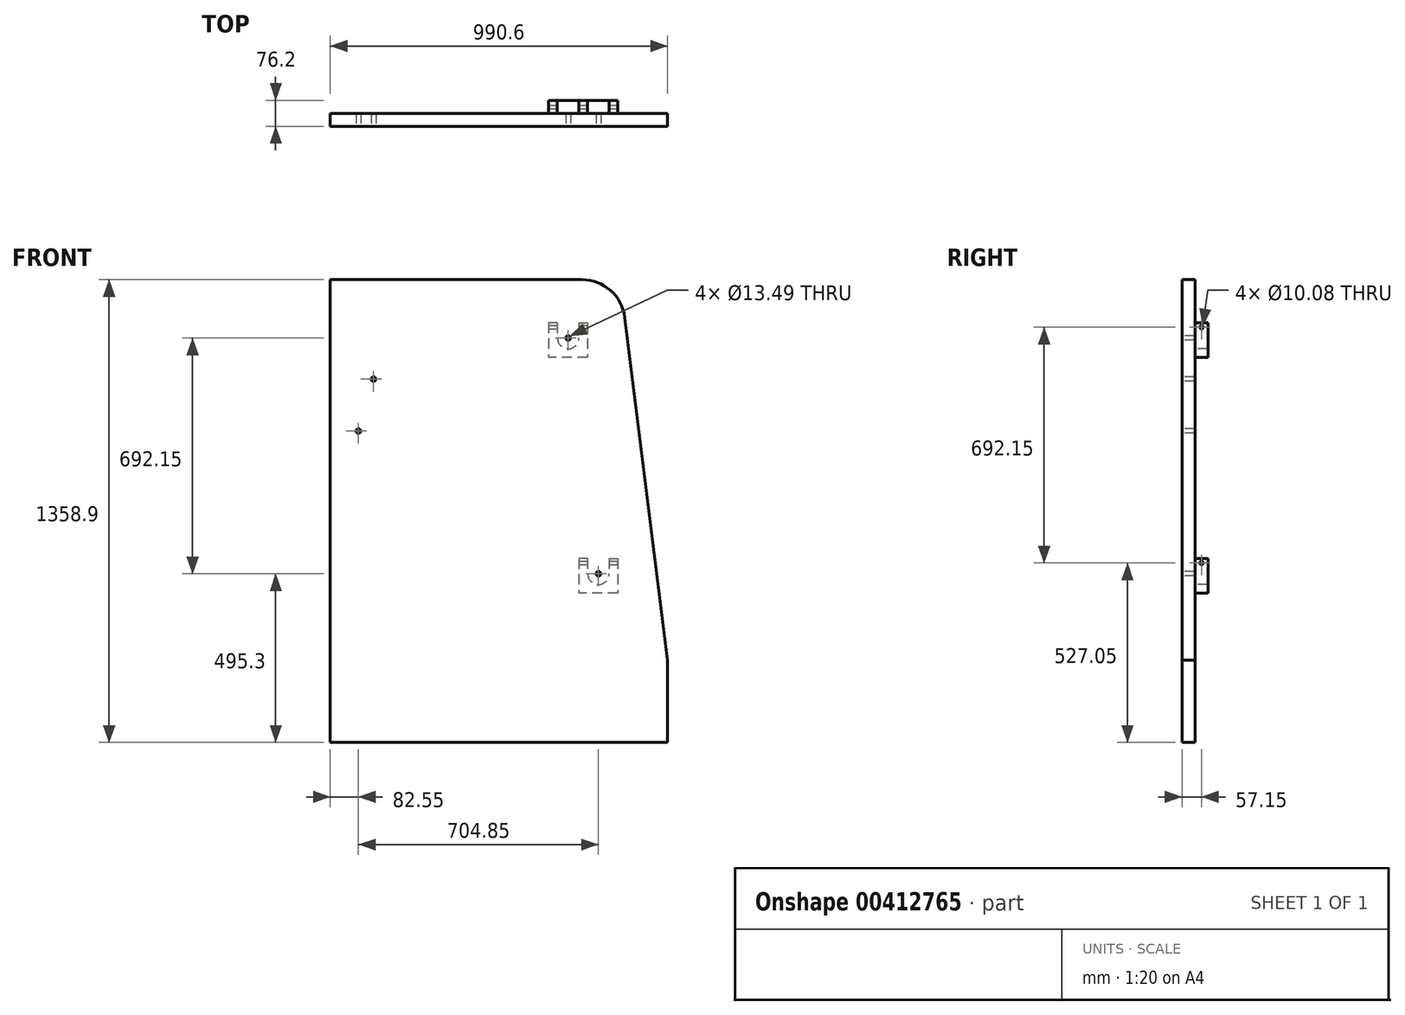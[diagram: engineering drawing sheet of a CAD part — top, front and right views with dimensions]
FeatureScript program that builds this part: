
annotation { "Feature Type Name" : "Feature", "Feature Type Description" : "" }
export const myFeature = defineFeature(function(context is Context, id is Id, definition is map)
    precondition{}
    {
        {
            var Q0;
            Q0=qCreatedBy(makeId("Front.planeOp"),FACE);
            var sketch = newSketch(context, id + "F0", { "sketchPlane" : qUnion([Q0])});
            skLineSegment(sketch, "E0", {"start": v(0, 0) * mm, "end": v(0, 1358.9) * mm});
            skLineSegment(sketch, "E1", {"start": v(990.6, 0) * mm, "end": v(0, 0) * mm});
            skLineSegment(sketch, "E2", {"start": v(990.6, 0) * mm, "end": v(990.6, 241.3) * mm});
            skLineSegment(sketch, "E3", {"start": v(990.6, 241.3) * mm, "end": v(864.8, 1247.65) * mm});
            skLineSegment(sketch, "E4", {"start": v(738.79, 1358.9) * mm, "end": v(0, 1358.9) * mm});
            skPoint(sketch, "E5.visualSharp", {"position": v(850.9, 1358.9) * mm});
            skArc(sketch, "E5.filletArc", {"start": v(864.8, 1247.65) * mm, "mid": v(822.84, 1327.1) * mm, "end": v(738.79, 1358.9) * mm});
            skSolve(sketch);
        }
        {
            var Q0;
            Q0 = qSketchRegion(id + "F0", true);
            extrude(context, id + "F1", {"entities" : qUnion([Q0]), "depth" : 38.1 * mm, "offsetDistance" : 25.4 * mm});
        }
        {
            var Q0;
            Q0=makeQuery(id+"F1.opExtrude","CAP_FACE",FACE,{"disambiguationData":[OSD([sQuery(id+"F0.wireOp",EDGE,"E0"),sQuery(id+"F0.wireOp",EDGE,"E1"),sQuery(id+"F0.wireOp",EDGE,"E2"),sQuery(id+"F0.wireOp",EDGE,"E3"),sQuery(id+"F0.wireOp",EDGE,"E4"),sQuery(id+"F0.wireOp",EDGE,"E5.filletArc")])],"isStart":false});
            var sketch = newSketch(context, id + "F2", { "sketchPlane" : qUnion([Q0])});
            skPoint(sketch, "E6", {"position": v(698.5, 1187.45) * mm});
            skPoint(sketch, "E7", {"position": v(787.4, 495.3) * mm});
            skPoint(sketch, "E8", {"position": v(82.55, 914.4) * mm});
            skPoint(sketch, "E9", {"position": v(127, 1066.8) * mm});
            skSolve(sketch);
        }
        {
            var Q0;
            Q0=sQuery(id+"F2.wireOp",VERTEX,"E6");
            var Q1;
            Q1=sQuery(id+"F2.wireOp",VERTEX,"E8");
            var Q2;
            Q2=sQuery(id+"F2.wireOp",VERTEX,"E9");
            var Q3;
            Q3=sQuery(id+"F2.wireOp",VERTEX,"E7");
            var Q4;
            Q4=makeQuery(id+"F1.opExtrude","SWEPT_BODY",BODY,{"disambiguationData":[OSD([sQuery(id+"F0.wireOp",EDGE,"E0"),sQuery(id+"F0.wireOp",EDGE,"E1"),sQuery(id+"F0.wireOp",EDGE,"E2"),sQuery(id+"F0.wireOp",EDGE,"E3"),sQuery(id+"F0.wireOp",EDGE,"E4"),sQuery(id+"F0.wireOp",EDGE,"E5.filletArc")])]});
            hole(context, id + "F3", {"style" : HoleStyle.SIMPLE, "endStyle" : HoleEndStyle.THROUGH, "standardTappedOrClearance" : lookupTablePath({ "standard" : "ANSI", "fit" : "Normal (ASME)", "size" : "1/2", "type" : "Clearance" }), "standardBlindInLast" : lookupTablePath({ "fit" : "Free", "standard" : "ANSI", "size" : "1/2", "type" : "Clearance" }), "holeDiameter" : 13.5 * mm, "tappedDepth" : 20.65 * mm, "tapClearance" : 3, "startFromSketch" : true, "locations" : qUnion([Q0, Q1, Q2, Q3]), "scope" : qUnion([Q4])});
        }
        {
            var Q0;
            Q0=makeQuery(id+"F1.opExtrude","CAP_FACE",FACE,{"disambiguationData":[OSD([sQuery(id+"F0.wireOp",EDGE,"E0"),sQuery(id+"F0.wireOp",EDGE,"E1"),sQuery(id+"F0.wireOp",EDGE,"E2"),sQuery(id+"F0.wireOp",EDGE,"E3"),sQuery(id+"F0.wireOp",EDGE,"E4"),sQuery(id+"F0.wireOp",EDGE,"E5.filletArc")])],"isStart":true});
            var sketch = newSketch(context, id + "F4", { "sketchPlane" : qUnion([Q0])});
            skArc(sketch, "E10", {"start": v(-730.25, 1187.45) * mm, "mid": v(-698.5, 1155.7) * mm, "end": v(-666.75, 1187.45) * mm});
            skLineSegment(sketch, "E11", {"start": v(-730.25, 1231.9) * mm, "end": v(-730.25, 1187.45) * mm});
            skLineSegment(sketch, "E12", {"start": v(-698.5, 1250.76) * mm, "end": v(-698.5, 1118.92) * mm, "construction": true});
            skLineSegment(sketch, "E13.MirrorCS", {"start": v(-666.75, 1231.9) * mm, "end": v(-666.75, 1187.45) * mm});
            skLineSegment(sketch, "E14", {"start": v(-730.25, 1231.9) * mm, "end": v(-755.65, 1231.9) * mm});
            skLineSegment(sketch, "E15", {"start": v(-755.65, 1231.9) * mm, "end": v(-755.65, 1130.3) * mm});
            skLineSegment(sketch, "E16", {"start": v(-755.65, 1130.3) * mm, "end": v(-698.5, 1130.3) * mm});
            skLineSegment(sketch, "E17.MirrorCS", {"start": v(-641.35, 1130.3) * mm, "end": v(-698.5, 1130.3) * mm});
            skLineSegment(sketch, "E18.MirrorCS", {"start": v(-641.35, 1231.9) * mm, "end": v(-641.35, 1130.3) * mm});
            skLineSegment(sketch, "E19.MirrorCS", {"start": v(-666.75, 1231.9) * mm, "end": v(-641.35, 1231.9) * mm});
            skPoint(sketch, "E20.MirrorCS.start.orphan", {"position": v(-698.5, 1219.2) * mm});
            skPoint(sketch, "E21.start.orphan", {"position": v(-698.5, 1155.7) * mm});
            skSolve(sketch);
        }
        {
            var Q0;
            Q0 = qSketchRegion(id + "F4", true);
            extrude(context, id + "F5", {"entities" : qUnion([Q0]), "operationType" : NewBodyOperationType.ADD, "depth" : 38.1 * mm, "offsetDistance" : 25.4 * mm});
        }
        {
            var Q0;
            Q0=makeQuery(id+"F1.opExtrude","CAP_FACE",FACE,{"disambiguationData":[OSD([sQuery(id+"F0.wireOp",EDGE,"E0"),sQuery(id+"F0.wireOp",EDGE,"E1"),sQuery(id+"F0.wireOp",EDGE,"E2"),sQuery(id+"F0.wireOp",EDGE,"E3"),sQuery(id+"F0.wireOp",EDGE,"E4"),sQuery(id+"F0.wireOp",EDGE,"E5.filletArc")])],"isStart":true});
            var sketch = newSketch(context, id + "F6", { "sketchPlane" : qUnion([Q0])});
            skArc(sketch, "E22", {"start": v(-819.15, 495.3) * mm, "mid": v(-787.4, 463.55) * mm, "end": v(-755.65, 495.3) * mm});
            skLineSegment(sketch, "E23", {"start": v(-819.15, 539.75) * mm, "end": v(-819.15, 495.3) * mm});
            skLineSegment(sketch, "E24", {"start": v(-787.4, 529.49) * mm, "end": v(-787.4, 397.65) * mm, "construction": true});
            skLineSegment(sketch, "E25.MirrorCS", {"start": v(-755.65, 539.75) * mm, "end": v(-755.65, 495.3) * mm});
            skLineSegment(sketch, "E26", {"start": v(-819.15, 539.75) * mm, "end": v(-844.55, 539.75) * mm});
            skLineSegment(sketch, "E27", {"start": v(-844.55, 539.75) * mm, "end": v(-844.55, 438.15) * mm});
            skLineSegment(sketch, "E28", {"start": v(-844.55, 438.15) * mm, "end": v(-787.4, 438.15) * mm});
            skLineSegment(sketch, "E29.MirrorCS", {"start": v(-730.25, 438.15) * mm, "end": v(-787.4, 438.15) * mm});
            skLineSegment(sketch, "E30.MirrorCS", {"start": v(-730.25, 539.75) * mm, "end": v(-730.25, 438.15) * mm});
            skLineSegment(sketch, "E31.MirrorCS", {"start": v(-755.65, 539.75) * mm, "end": v(-730.25, 539.75) * mm});
            skPoint(sketch, "E32.MirrorCS.start.orphan", {"position": v(-787.4, 527.05) * mm});
            skPoint(sketch, "E33.start.orphan", {"position": v(-787.4, 463.55) * mm});
            skSolve(sketch);
        }
        {
            var Q0;
            Q0 = qSketchRegion(id + "F6", true);
            extrude(context, id + "F7", {"entities" : qUnion([Q0]), "operationType" : NewBodyOperationType.ADD, "depth" : 38.1 * mm, "offsetDistance" : 25.4 * mm});
        }
        {
            var Q0;
            Q0=makeQuery(id+"F5.opExtrude","SWEPT_FACE",FACE,{"disambiguationData":[OSD([sQuery(id+"F4.wireOp",EDGE,"E15")])]});
            var sketch = newSketch(context, id + "F8", { "sketchPlane" : qUnion([Q0])});
            skPoint(sketch, "E34", {"position": v(19.05, 1219.2) * mm});
            skPoint(sketch, "E34.positionSnap0", {"position": v(19.05, 1231.9) * mm});
            skSolve(sketch);
        }
        {
            var Q0;
            Q0=makeQuery(id+"F7.opExtrude","SWEPT_FACE",FACE,{"disambiguationData":[OSD([sQuery(id+"F6.wireOp",EDGE,"E27")])]});
            var sketch = newSketch(context, id + "F9", { "sketchPlane" : qUnion([Q0])});
            skPoint(sketch, "E35", {"position": v(19.05, 527.05) * mm});
            skPoint(sketch, "E35.positionSnap0", {"position": v(19.05, 539.75) * mm});
            skSolve(sketch);
        }
        {
            var Q0;
            Q0=sQuery(id+"F8.wireOp",VERTEX,"E34");
            var Q1;
            Q1=sQuery(id+"F9.wireOp",VERTEX,"E35");
            var Q2;
            Q2=makeQuery(id+"F1.opExtrude","SWEPT_BODY",BODY,{"disambiguationData":[OSD([sQuery(id+"F0.wireOp",EDGE,"E0"),sQuery(id+"F0.wireOp",EDGE,"E1"),sQuery(id+"F0.wireOp",EDGE,"E2"),sQuery(id+"F0.wireOp",EDGE,"E3"),sQuery(id+"F0.wireOp",EDGE,"E4"),sQuery(id+"F0.wireOp",EDGE,"E5.filletArc")])]});
            hole(context, id + "F10", {"style" : HoleStyle.SIMPLE, "endStyle" : HoleEndStyle.THROUGH, "standardTappedOrClearance" : lookupTablePath({ "standard" : "ANSI", "fit" : "Normal (ASME)", "size" : "3/8", "type" : "Clearance" }), "standardBlindInLast" : lookupTablePath({ "fit" : "Free", "standard" : "ANSI", "size" : "3/8", "type" : "Clearance" }), "holeDiameter" : 10.08 * mm, "tappedDepth" : 20.65 * mm, "tapClearance" : 3, "startFromSketch" : true, "locations" : qUnion([Q0, Q1]), "scope" : qUnion([Q2])});
        }
    });
